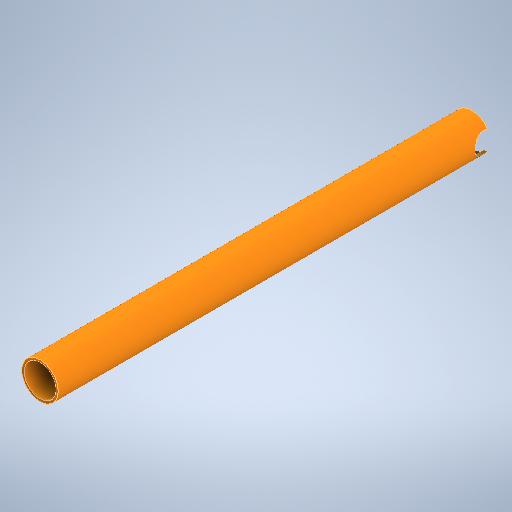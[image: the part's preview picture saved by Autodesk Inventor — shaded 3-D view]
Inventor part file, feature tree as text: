
AUTODESK INVENTOR PART (.ipt)
format: ipt  version: 2025.1 (Build 291241000, 241)  size: 271,360 bytes
history: native  units: mm
features: sketch x3, revolve x1, hole x1, plane x1, extrude x1, projected_geometry x1
ambient origin geometry x8: Origin, YZ Plane, XZ Plane, XY Plane, X Axis, Y Axis, Z Axis, Center Point
bodies: Solid1 (feature_tree)
feature tree (8):
  revolve  "Revolution1"  [1 undecoded]
  hole  "Hole1"  [1 undecoded]
  plane  "Work Plane1"
  extrude  "Extrusion1"  Depth=10.0mm
  sketch  "Sketch1"  dims[d0=22.0mm d1=260.0mm]
  sketch  "Sketch2"  dims[d2=90.0deg]
  sketch  "Sketch3"  dims[d3=19.0mm d4=6.0mm d5=4.0mm d6=2.0mm d7=90.0deg d8=8.0mm d9=0.0mm d10=11.0mm d11=3.0mm d12=6.0mm d13=10.0mm d14=0.0mm]
  projected_geometry  "Projected Loop1"
note: 2 required parameter values undecoded (feature->parameter linkage not recoverable at this tier; creation-order binding heuristic only, values carry confidence <= 0.55)